# Revit family: STH21940BR_30_40_STH21940PTO_30
name_source: partatom
category: Luminárias
units: mm (PartAtom-declared; Revit-internal decimal feet)

## family parameters
Compartilhado = Não
Corte com vazios quando carregada = Não
Cota do conector redondo = Utilizar diâmetro
Fonte luminosa = Sim
Hospedeiro = Forro
Manter orientação da anotação = Não
Número OmniClass = 23.80.70.11
Ponto de cálculo do ambiente = Não
Sempre na vertical = Sim
Tipo de parte = Normal
Título OmniClass = Luminaries for Internal Lighting

## types (3) — shared parameters
Altura = 0.07 m
Comprimento = 0.14 m
Cromado = Cromado
Dimerização = Não dimerizável
Fabricante = Stella
Filtro de cor = 16777215
Grau de proteção (IP) = IP20
IRC (Índice de reprodução de cores) = >80
Largura = 0.14 m
Modelo = Easy PAR30 Evo
Potência = 12 W
Tensão Elétrica = 100V-240V
Troca de temperatura da cor de lâmpada com esmaecimento = <Nenhum>
URL = https://stella.com.br
Vidro = Vidro
Ângulo de Abertura = 30°
Ângulo de inclinação = 90.00°
zero-valued in all types: Elevação padrão

## per-type parameters (varying)
| type | Arquivo de rede fotométrica | Estrutura | Fluxo Luminoso | Luminoso | Referência | Temperatura da cor (K) |
| STH21940BR/30 - BRANCO - BIVOLT - 3000K - 990lm - 30° | STELLA - STH21940BR-30 - EASY PAR30 EMBUTIDO RECUADO DIRECIONÁVEL.ies | Al - Branco | 990 lm | Luminoso - 3000K | STH21940BR/30 | 3000 K |
| STH21940BR/40 - BRANCO - BIVOLT - 4000K - 1000lm - 30° | STELLA - STH21940BR-40 - EASY PAR30 EMBUTIDO RECUADO DIRECIONÁVEL.ies | Al - Branco | 1000 lm | Luminoso - 4000K | STH21940BR/40 | 4000 K |
| STH21940PTO/30 - PRETO - BIVOLT - 3000K - 970lm - 30° | STELLA - STH21940PTO-30 - EASY PAR30 EMBUTIDO RECUADO DIRECIONÁVEL .ies | Al - Preto | 970 lm | Luminoso - 3000K | STH21940PTO/30 | 3000 K |
